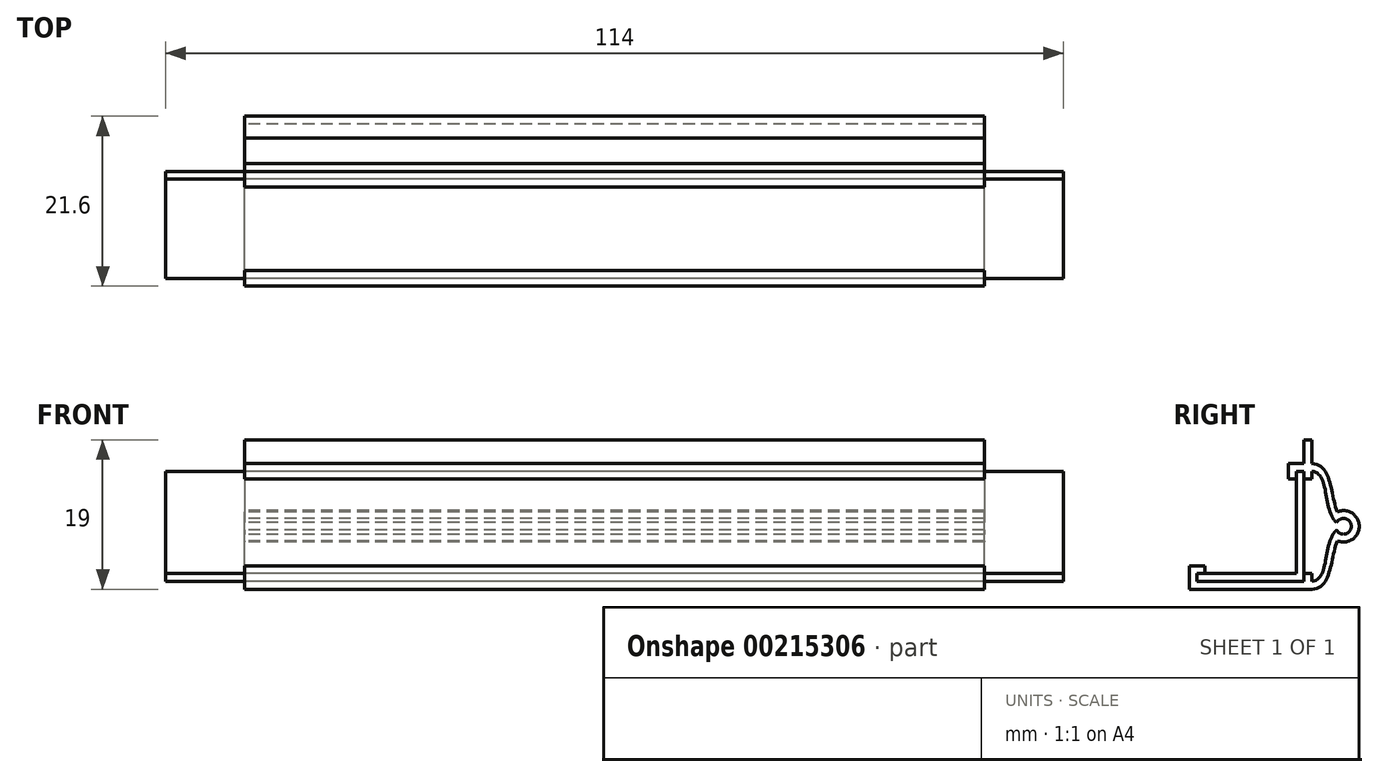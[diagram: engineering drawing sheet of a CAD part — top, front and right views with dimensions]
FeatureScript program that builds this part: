
annotation { "Feature Type Name" : "Feature", "Feature Type Description" : "" }
export const myFeature = defineFeature(function(context is Context, id is Id, definition is map)
    precondition{}
    {
        {
            assignVariable(context, id + "F0", {"name" : "strip_length", "anyValue" : 94});
        }
        {
            var Q0;
            Q0=qCreatedBy(makeId("Right.planeOp"),FACE);
            var sketch = newSketch(context, id + "F1", { "sketchPlane" : qUnion([Q0])});
            skLineSegment(sketch, "E0", {"start": v(-6.8, 0) * mm, "end": v(6.8, 0) * mm});
            skPoint(sketch, "E1", {"position": v(0, 0) * mm});
            skLineSegment(sketch, "E2", {"start": v(6.8, 0) * mm, "end": v(6.8, 14) * mm});
            skLineSegment(sketch, "E3.0", {"start": v(5.8, 1) * mm, "end": v(5.8, 14) * mm});
            skLineSegment(sketch, "E3.1", {"start": v(-6.8, 1) * mm, "end": v(5.8, 1) * mm});
            skLineSegment(sketch, "E4", {"start": v(-6.8, 1) * mm, "end": v(-6.8, 0) * mm});
            skLineSegment(sketch, "E5", {"start": v(5.8, 14) * mm, "end": v(6.8, 14) * mm});
            skSolve(sketch);
        }
        {
            var Q0;
            Q0=makeQuery(id+"F1.imprint","IMPRINT",FACE,{"disambiguationData":[TD([[makeQuery(id+"F1.imprint","IMPRINT",EDGE,{"derivedFrom":sQuery(id+"F1.wireOp",EDGE,"E0")}),1.0]])]});
            extrude(context, id + "F2", {"entities" : qUnion([Q0]), "endBound" : BoundingType.SYMMETRIC, "depth" : (getVariable(context, 'strip_length') + 2 * 10) * mm});
        }
        {
            var Q0;
            Q0=qCreatedBy(makeId("Right.planeOp"),FACE);
            var sketch = newSketch(context, id + "F3", { "sketchPlane" : qUnion([Q0])});
            skPoint(sketch, "E6.0", {"position": v(5.8, 14) * mm});
            skPoint(sketch, "E7.0", {"position": v(6.8, 14) * mm});
            skPoint(sketch, "E8.0", {"position": v(6.8, 0) * mm});
            skPoint(sketch, "E9.0", {"position": v(-6.8, 0) * mm});
            skPoint(sketch, "E10.0", {"position": v(-6.8, 1) * mm});
            skLineSegment(sketch, "E11.0", {"start": v(5.8, 15) * mm, "end": v(7.8, 15) * mm});
            skLineSegment(sketch, "E11.1", {"start": v(7.8, -1) * mm, "end": v(7.8, 15) * mm});
            skLineSegment(sketch, "E11.2", {"start": v(-7.8, -1) * mm, "end": v(7.8, -1) * mm});
            skLineSegment(sketch, "E11.3", {"start": v(-7.8, 1) * mm, "end": v(-7.8, -1) * mm});
            skLineSegment(sketch, "E12", {"start": v(5.8, 15) * mm, "end": v(4.8, 15) * mm});
            skLineSegment(sketch, "E13", {"start": v(4.8, 15) * mm, "end": v(4.8, 13) * mm});
            skLineSegment(sketch, "E14", {"start": v(-7.8, 1) * mm, "end": v(-7.8, 2) * mm});
            skLineSegment(sketch, "E15", {"start": v(-7.8, 2) * mm, "end": v(-5.8, 2) * mm});
            skLineSegment(sketch, "E16", {"start": v(-5.8, 1) * mm, "end": v(-5.8, 2) * mm});
            skLineSegment(sketch, "E17", {"start": v(-5.8, 1) * mm, "end": v(-6.8, 1) * mm});
            skLineSegment(sketch, "E18", {"start": v(-6.8, 1) * mm, "end": v(-6.8, 0) * mm});
            skLineSegment(sketch, "E19", {"start": v(-6.8, 0) * mm, "end": v(6.8, 0) * mm});
            skLineSegment(sketch, "E20", {"start": v(6.8, 0) * mm, "end": v(6.8, 14) * mm});
            skLineSegment(sketch, "E21", {"start": v(6.8, 14) * mm, "end": v(5.8, 14) * mm});
            skLineSegment(sketch, "E22", {"start": v(5.8, 14) * mm, "end": v(5.8, 13) * mm});
            skLineSegment(sketch, "E23", {"start": v(4.8, 13) * mm, "end": v(5.8, 13) * mm});
            skLineSegment(sketch, "E24", {"start": v(7.8, 15) * mm, "end": v(7.8, 18) * mm});
            skLineSegment(sketch, "E25", {"start": v(7.8, 18) * mm, "end": v(6.8, 18) * mm});
            skPoint(sketch, "E25.endSnap0", {"position": v(6.8, 15) * mm});
            skLineSegment(sketch, "E26", {"start": v(6.8, 18) * mm, "end": v(6.8, 15) * mm});
            skPoint(sketch, "E27", {"position": v(4.8, 14) * mm});
            skLineSegment(sketch, "E28", {"start": v(6.8, 14) * mm, "end": v(7.8, 14) * mm});
            skLineSegment(sketch, "E29", {"start": v(6.8, 0) * mm, "end": v(7.8, 0) * mm});
            skPoint(sketch, "E30", {"position": v(7.8, 7) * mm});
            skLineSegment(sketch, "E31", {"start": v(7.8, 14) * mm, "end": v(11.8, 7) * mm, "construction": true});
            skLineSegment(sketch, "E32", {"start": v(11.8, 7) * mm, "end": v(7.8, 0) * mm, "construction": true});
            skFitSpline(sketch, "E33", {"points": [v(7.8, 14) * mm, v(11.8, 7) * mm], "startDerivative": vector(7.92, -0.89) * mm, "endDerivative": vector(9.07, -2.31) * mm});
            skLineSegment(sketch, "E34", {"start": v(7.8, 7) * mm, "end": v(11.8, 7) * mm, "construction": true});
            skFitSpline(sketch, "E35.MirrorCS", {"points": [v(7.8, 0) * mm, v(11.8, 7) * mm], "startDerivative": vector(7.92, 0.89) * mm, "endDerivative": vector(9.07, 2.31) * mm});
            skLineSegment(sketch, "E36", {"start": v(11.8, 7) * mm, "end": v(12.8, 7) * mm, "construction": true});
            skFitSpline(sketch, "E37", {"points": [v(7.8, 15) * mm, v(12.8, 7) * mm], "startDerivative": vector(10.62, -0.87) * mm, "endDerivative": vector(10.23, -3.7) * mm});
            skFitSpline(sketch, "E38.MirrorCS", {"points": [v(7.8, -1) * mm, v(12.8, 7) * mm], "startDerivative": vector(10.62, 0.87) * mm, "endDerivative": vector(10.23, 3.7) * mm});
            skLineSegment(sketch, "E39", {"start": v(12.8, 7) * mm, "end": v(13.8, 7) * mm, "construction": true});
            skCircle(sketch, "E40", {"center": v(11.8, 7) * mm, "radius": 1 * mm});
            skCircle(sketch, "E41", {"center": v(11.8, 7) * mm, "radius": 2 * mm});
            skLineSegment(sketch, "E42", {"start": v(6.8, 13) * mm, "end": v(7.8, 13) * mm});
            skLineSegment(sketch, "E43", {"start": v(6.8, 1) * mm, "end": v(7.8, 1) * mm});
            skSolve(sketch);
        }
        {
            var Q0;
            Q0=makeQuery(id+"F3.imprint","IMPRINT",FACE,{"disambiguationData":[TD([[makeQuery(id+"F3.imprint","IMPRINT",EDGE,{"derivedFrom":sQuery(id+"F3.wireOp",EDGE,"E11.0")}),-1.0]])]});
            var Q1;
            {var subQ0=sQuery(id+"F3.wireOp",EDGE,"E24");Q1=makeQuery(id+"F3.imprint","IMPRINT",FACE,{"disambiguationData":[TD([[makeQuery(id+"F3.imprint","IMPRINT",EDGE,{"derivedFrom":subQ0}),1.0]])]});}
            var Q2;
            {var subQ0=sQuery(id+"F3.wireOp",EDGE,"E37");var subQ5=sQuery(id+"F3.wireOp",EDGE,"E41");var subQ6=makeQuery(id+"F3.imprint","INTERSECT",VERTEX,{"derivedFrom":[subQ0,subQ5]});Q2=makeQuery(id+"F3.imprint","IMPRINT",FACE,{"disambiguationData":[TD([[makeQuery(id+"F3.imprint","IMPRINT",EDGE,{"disambiguationData":[TD([[subQ6,-1.0]])],"derivedFrom":subQ5}),-1.0]])]});}
            var Q3;
            {var subQ0=sQuery(id+"F3.wireOp",EDGE,"E41");var subQ1=sQuery(id+"F3.wireOp",EDGE,"E33");var subQ2=makeQuery(id+"F3.imprint","INTERSECT",VERTEX,{"derivedFrom":[subQ1,subQ0]});Q3=makeQuery(id+"F3.imprint","IMPRINT",FACE,{"disambiguationData":[TD([[makeQuery(id+"F3.imprint","IMPRINT",EDGE,{"disambiguationData":[TD([[subQ2,-1.0]])],"derivedFrom":subQ1}),1.0]])]});}
            var Q4;
            {var subQ2=sQuery(id+"F3.wireOp",EDGE,"E37");var subQ5=sQuery(id+"F3.wireOp",EDGE,"E41");var subQ8=makeQuery(id+"F3.imprint","INTERSECT",VERTEX,{"derivedFrom":[subQ2,subQ5]});Q4=makeQuery(id+"F3.imprint","IMPRINT",FACE,{"disambiguationData":[TD([[makeQuery(id+"F3.imprint","IMPRINT",EDGE,{"disambiguationData":[TD([[subQ8,-1.0]])],"derivedFrom":subQ2}),1.0]])]});}
            var Q5;
            {var subQ0=sQuery(id+"F3.wireOp",EDGE,"E41");var subQ1=sQuery(id+"F3.wireOp",EDGE,"E35.MirrorCS");var subQ2=makeQuery(id+"F3.imprint","INTERSECT",VERTEX,{"derivedFrom":[subQ1,subQ0]});Q5=makeQuery(id+"F3.imprint","IMPRINT",FACE,{"disambiguationData":[TD([[makeQuery(id+"F3.imprint","IMPRINT",EDGE,{"disambiguationData":[TD([[subQ2,-1.0]])],"derivedFrom":subQ1}),-1.0]])]});}
            var Q6;
            {var subQ0=sQuery(id+"F3.wireOp",EDGE,"E38.MirrorCS");var subQ5=sQuery(id+"F3.wireOp",EDGE,"E41");var subQ6=makeQuery(id+"F3.imprint","INTERSECT",VERTEX,{"derivedFrom":[subQ0,subQ5]});Q6=makeQuery(id+"F3.imprint","IMPRINT",FACE,{"disambiguationData":[TD([[makeQuery(id+"F3.imprint","IMPRINT",EDGE,{"disambiguationData":[TD([[subQ6,1.0]])],"derivedFrom":subQ5}),-1.0]])]});}
            var Q7;
            {var subQ0=sQuery(id+"F3.wireOp",EDGE,"E11.2");Q7=makeQuery(id+"F3.imprint","IMPRINT",FACE,{"disambiguationData":[TD([[makeQuery(id+"F3.imprint","IMPRINT",EDGE,{"derivedFrom":subQ0}),1.0]])]});}
            var Q8;
            {var subQ0=sQuery(id+"F3.wireOp",EDGE,"E28");Q8=makeQuery(id+"F3.imprint","IMPRINT",FACE,{"disambiguationData":[TD([[makeQuery(id+"F3.imprint","IMPRINT",EDGE,{"derivedFrom":subQ0}),-1.0]])]});}
            var Q9;
            {var subQ0=sQuery(id+"F3.wireOp",EDGE,"E29");Q9=makeQuery(id+"F3.imprint","IMPRINT",FACE,{"disambiguationData":[TD([[makeQuery(id+"F3.imprint","IMPRINT",EDGE,{"derivedFrom":subQ0}),1.0]])]});}
            extrude(context, id + "F4", {"entities" : qUnion([Q0, Q1, Q2, Q3, Q4, Q5, Q6, Q7, Q8, Q9]), "endBound" : BoundingType.SYMMETRIC, "depth" : (getVariable(context, 'strip_length')) * mm});
        }
    });
